# Revit family: Ceiling-Fan_VCDK 010-015C_Carnes
name_source: partatom
category: Mechanical Equipment
revit_build: Autodesk Revit Architecture 2012 (Build: 20110309_2315(x64)
units: mm (PartAtom-declared; Revit-internal decimal feet)

## types (1)
- Ceiling-Fan_VCDK 010-015C_Carnes
    04 CSI = 23 37 13
    95 CSI = 15850
    Assembly Code = D3040200
    Box Depth = 0' - 8 13/16"
    Box Size = 10.25" Sq.
    Catalog URL = http://www.carnes.com
    Description = Ceiling Ventilators
    Duct Connector = 6"
    Duct Radius = 0' - 3"
    Grill = Aluminum-Carnes-Spun-Brushed
    Grill Depth = 0' - 0 3/8"
    Grill Size = 12 5/8 Sq.
    Housing = Aluminum-Carnes-Spun-Brushed
    IOM Instructions URL = http://www.carnes.com
    Manufacturer = CARNES COMPANY
    Manufacturer Fax = 608-845-6470
    Model = VCDK 010-015C
    Parts List URL = http://www.carnes.com
    Product Page URL = http://www.carnes.com
    URL = http://www.carnes.com
    Warranty URL = http://www.carnes.com
    ecoScorecard Product Page = http://ecoscorecard.com

## geometry (parser evidence)
native form markers: Blend x4, Sweep x2
no freeform markers — native parametric forms only
